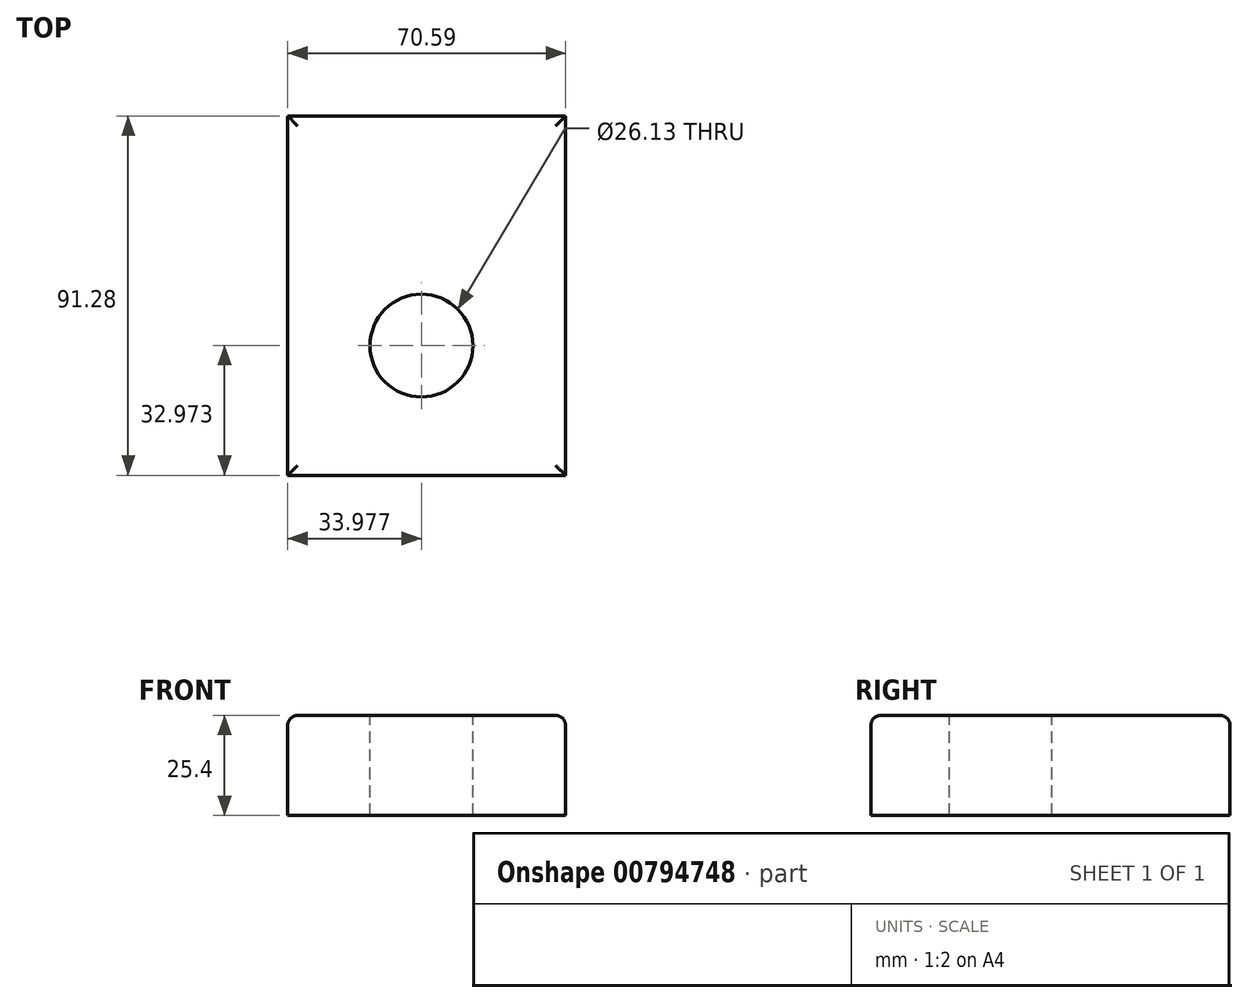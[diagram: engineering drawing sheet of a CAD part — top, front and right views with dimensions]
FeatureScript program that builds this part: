
annotation { "Feature Type Name" : "Feature", "Feature Type Description" : "" }
export const myFeature = defineFeature(function(context is Context, id is Id, definition is map)
    precondition{}
    {
        {
            var Q0;
            Q0=qCreatedBy(makeId("Top.planeOp"),FACE);
            var sketch = newSketch(context, id + "F0", { "sketchPlane" : qUnion([Q0])});
            skLineSegment(sketch, "E0.bottom", {"start": v(-25.5, -44.35) * mm, "end": v(45.09, -44.35) * mm});
            skLineSegment(sketch, "E0.top", {"start": v(-25.5, 46.93) * mm, "end": v(45.09, 46.93) * mm});
            skLineSegment(sketch, "E0.left", {"start": v(-25.5, -44.35) * mm, "end": v(-25.5, 46.93) * mm});
            skLineSegment(sketch, "E0.right", {"start": v(45.09, -44.35) * mm, "end": v(45.09, 46.93) * mm});
            skSolve(sketch);
        }
        {
            var Q0;
            Q0=makeQuery(id+"F0.imprint","IMPRINT",FACE,{"disambiguationData":[TD([[makeQuery(id+"F0.imprint","IMPRINT",EDGE,{"derivedFrom":sQuery(id+"F0.wireOp",EDGE,"E0.bottom")}),1.0]])]});
            extrude(context, id + "F1", {"entities" : qUnion([Q0]), "depth" : 25.4 * mm, "offsetDistance" : 25.4 * mm});
        }
        {
            var Q0;
            Q0=makeQuery(id+"F1.opExtrude","CAP_EDGE",EDGE,{"disambiguationData":[OSD([sQuery(id+"F0.wireOp",EDGE,"E0.right")])],"isStart":false});
            var Q1;
            Q1=makeQuery(id+"F1.opExtrude","CAP_EDGE",EDGE,{"disambiguationData":[OSD([sQuery(id+"F0.wireOp",EDGE,"E0.top")])],"isStart":false});
            var Q2;
            Q2=makeQuery(id+"F1.opExtrude","CAP_EDGE",EDGE,{"disambiguationData":[OSD([sQuery(id+"F0.wireOp",EDGE,"E0.left")])],"isStart":false});
            var Q3;
            Q3=makeQuery(id+"F1.opExtrude","CAP_EDGE",EDGE,{"disambiguationData":[OSD([sQuery(id+"F0.wireOp",EDGE,"E0.bottom")])],"isStart":false});
            fillet(context, id + "F2", {"entities" : qUnion([Q0, Q1, Q2, Q3]), "radius" : 2.54 * mm, "tangentPropagation" : true, "allowEdgeOverflow" : false});
        }
        {
            var Q0;
            Q0=makeQuery(id+"F1.opExtrude","CAP_FACE",FACE,{"disambiguationData":[OSD([sQuery(id+"F0.wireOp",EDGE,"E0.bottom"),sQuery(id+"F0.wireOp",EDGE,"E0.top"),sQuery(id+"F0.wireOp",EDGE,"E0.left"),sQuery(id+"F0.wireOp",EDGE,"E0.right")])],"isStart":false});
            var sketch = newSketch(context, id + "F3", { "sketchPlane" : qUnion([Q0])});
            skCircle(sketch, "E1", {"center": v(8.48, -11.38) * mm, "radius": 13.06 * mm});
            skSolve(sketch);
        }
        {
            var Q0;
            Q0 = qSketchRegion(id + "F3", true);
            extrude(context, id + "F4", {"entities" : qUnion([Q0]), "operationType" : NewBodyOperationType.REMOVE, "oppositeDirection" : true, "depth" : 25.4 * mm, "offsetDistance" : 25.4 * mm});
        }
    });
